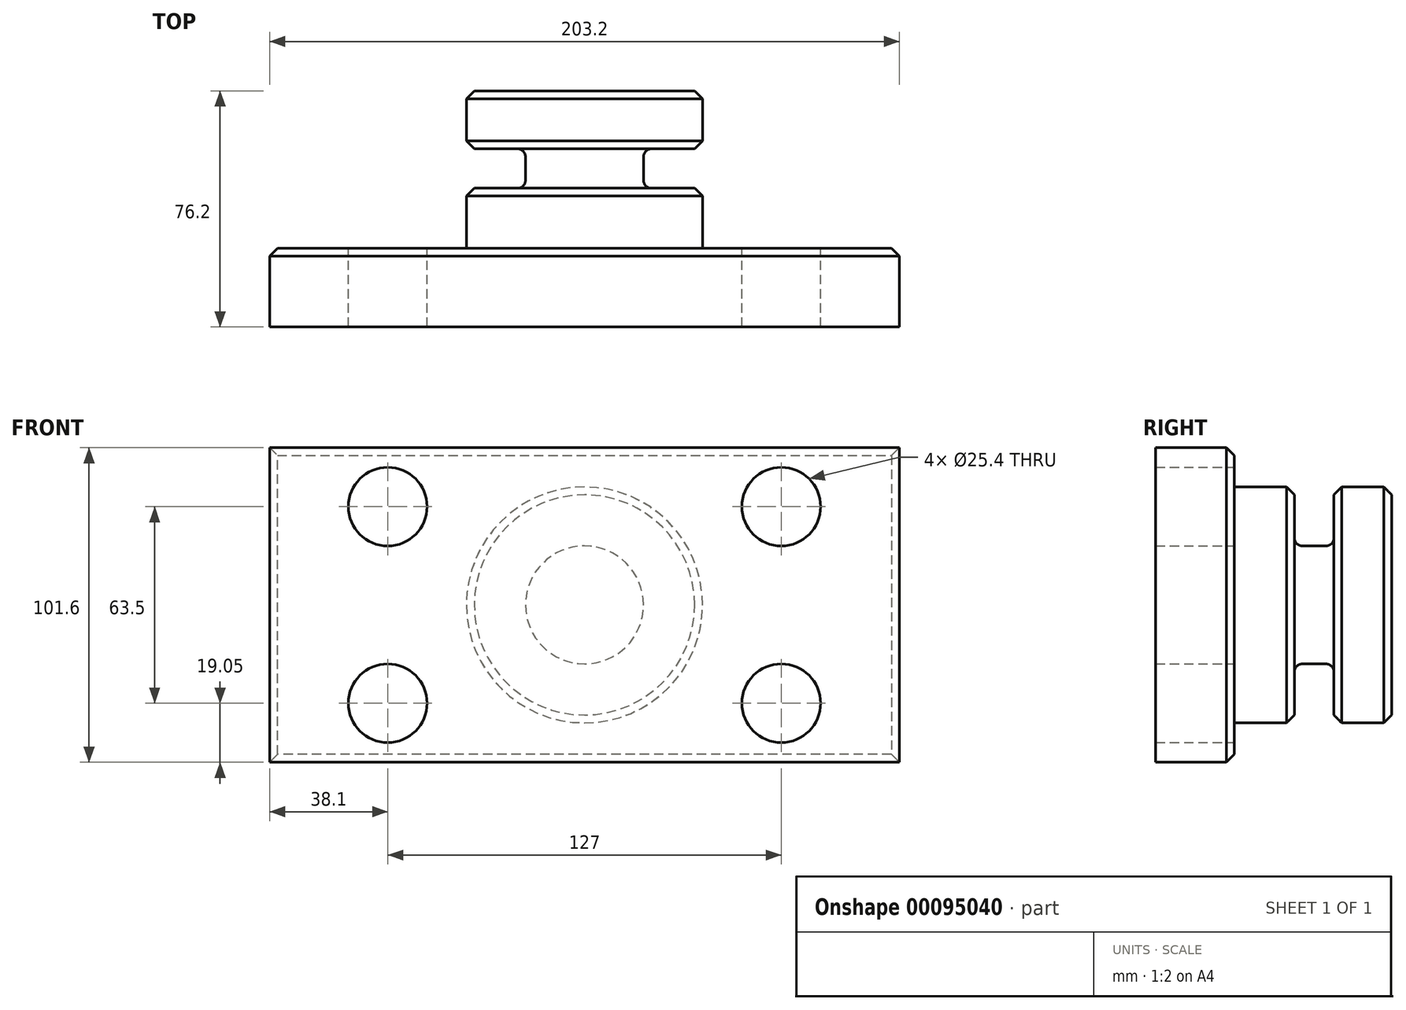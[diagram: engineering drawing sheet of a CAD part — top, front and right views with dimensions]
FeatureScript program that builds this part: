
annotation { "Feature Type Name" : "Feature", "Feature Type Description" : "" }
export const myFeature = defineFeature(function(context is Context, id is Id, definition is map)
    precondition{}
    {
        {
            var Q0;
            Q0=qCreatedBy(makeId("Front.planeOp"),FACE);
            var sketch = newSketch(context, id + "F0", { "sketchPlane" : qUnion([Q0])});
            skLineSegment(sketch, "E0.bottom", {"start": v(-101.6, 50.8) * mm, "end": v(101.6, 50.8) * mm});
            skLineSegment(sketch, "E0.top", {"start": v(-101.6, -50.8) * mm, "end": v(101.6, -50.8) * mm});
            skLineSegment(sketch, "E0.left", {"start": v(-101.6, 50.8) * mm, "end": v(-101.6, -50.8) * mm});
            skLineSegment(sketch, "E0.right", {"start": v(101.6, 50.8) * mm, "end": v(101.6, -50.8) * mm});
            skPoint(sketch, "E0.middle", {"position": v(0, 0) * mm});
            skSolve(sketch);
        }
        {
            var Q0;
            Q0 = qSketchRegion(id + "F0", true);
            extrude(context, id + "F1", {"entities" : qUnion([Q0]), "depth" : 25.4 * mm});
        }
        {
            var Q0;
            Q0=qCreatedBy(makeId("Front.planeOp"),FACE);
            var sketch = newSketch(context, id + "F2", { "sketchPlane" : qUnion([Q0])});
            skCircle(sketch, "E1", {"center": v(-63.5, 31.75) * mm, "radius": 12.7 * mm});
            skCircle(sketch, "E2", {"center": v(-63.5, -31.75) * mm, "radius": 12.7 * mm});
            skCircle(sketch, "E3", {"center": v(63.5, 31.75) * mm, "radius": 12.7 * mm});
            skCircle(sketch, "E4", {"center": v(63.5, -31.75) * mm, "radius": 12.7 * mm});
            skSolve(sketch);
        }
        {
            var Q0;
            Q0 = qSketchRegion(id + "F2", true);
            extrude(context, id + "F3", {"entities" : qUnion([Q0]), "operationType" : NewBodyOperationType.REMOVE, "depth" : 25.4 * mm});
        }
        {
            var Q0;
            Q0=qCreatedBy(makeId("Top.planeOp"),FACE);
            var sketch = newSketch(context, id + "F4", { "sketchPlane" : qUnion([Q0])});
            skLineSegment(sketch, "E5.bottom", {"start": v(0, 50.8) * mm, "end": v(-38.1, 50.8) * mm});
            skLineSegment(sketch, "E5.top", {"start": v(0, 0) * mm, "end": v(-38.1, 0) * mm});
            skLineSegment(sketch, "E5.left", {"start": v(0, 50.8) * mm, "end": v(0, 0) * mm});
            skLineSegment(sketch, "E5.right", {"start": v(-38.1, 50.8) * mm, "end": v(-38.1, 0) * mm});
            skSolve(sketch);
        }
        {
            var Q0;
            Q0 = qSketchRegion(id + "F4", true);
            var Q1;
            Q1=sQuery(id+"F4.wireOp",EDGE,"E5.left");
            revolve(context, id + "F5", {"operationType" : NewBodyOperationType.ADD, "entities" : qUnion([Q0]), "axis" : qUnion([Q1]), "revolveType" : RevolveType.FULL});
        }
        {
            var Q0;
            Q0=qCreatedBy(makeId("Top.planeOp"),FACE);
            var sketch = newSketch(context, id + "F6", { "sketchPlane" : qUnion([Q0])});
            skLineSegment(sketch, "E6.bottom", {"start": v(-44.45, 32.1) * mm, "end": v(-19.05, 32.1) * mm});
            skLineSegment(sketch, "E6.top", {"start": v(-44.45, 19.4) * mm, "end": v(-19.05, 19.4) * mm});
            skLineSegment(sketch, "E6.left", {"start": v(-44.45, 32.1) * mm, "end": v(-44.45, 19.4) * mm});
            skLineSegment(sketch, "E6.right", {"start": v(-19.05, 32.1) * mm, "end": v(-19.05, 19.4) * mm});
            skLineSegment(sketch, "E7", {"start": v(0, 0) * mm, "end": v(0, 134.13) * mm, "construction": true});
            skSolve(sketch);
        }
        {
            var Q0;
            Q0 = qSketchRegion(id + "F6", true);
            var Q1;
            Q1=sQuery(id+"F6.wireOp",EDGE,"E7");
            revolve(context, id + "F7", {"operationType" : NewBodyOperationType.REMOVE, "entities" : qUnion([Q0]), "axis" : qUnion([Q1]), "revolveType" : RevolveType.FULL, "oppositeDirection" : true});
        }
        {
            var Q0;
            Q0=makeQuery(id+"F5.opRevolve","SWEPT_EDGE",EDGE,{"disambiguationData":[OSD([sQuery(id+"F4.wireOp",EDGE,"E5.top"),sQuery(id+"F4.wireOp",EDGE,"E5.right")])]});
            var Q1;
            Q1=makeQuery(id+"F7.boolean.opBoolean","COPY",EDGE,{"derivedFrom":makeQuery(id+"F7.opRevolve","SWEPT_EDGE",EDGE,{"disambiguationData":[OSD([sQuery(id+"F6.wireOp",EDGE,"E6.top"),sQuery(id+"F6.wireOp",EDGE,"E6.right")])]})});
            var Q2;
            Q2=makeQuery(id+"F7.boolean.opBoolean","COPY",EDGE,{"derivedFrom":makeQuery(id+"F7.opRevolve","SWEPT_EDGE",EDGE,{"disambiguationData":[OSD([sQuery(id+"F6.wireOp",EDGE,"E6.bottom"),sQuery(id+"F6.wireOp",EDGE,"E6.right")])]})});
            fillet(context, id + "F8", {"entities" : qUnion([Q0, Q1, Q2]), "radius" : 2.54 * mm, "tangentPropagation" : true, "allowEdgeOverflow" : false});
        }
        {
            var Q0;
            Q0=makeQuery(id+"F5.opRevolve","SWEPT_EDGE",EDGE,{"disambiguationData":[OSD([sQuery(id+"F4.wireOp",EDGE,"E5.bottom"),sQuery(id+"F4.wireOp",EDGE,"E5.right")])]});
            var Q1;
            Q1=makeQuery(id+"F7.boolean.opBoolean","INTERSECT",EDGE,{"derivedFrom":[makeQuery(id+"F5.opRevolve","SWEPT_FACE",FACE,{"disambiguationData":[OSD([sQuery(id+"F4.wireOp",EDGE,"E5.right")])]}),makeQuery(id+"F7.opRevolve","SWEPT_FACE",FACE,{"disambiguationData":[OSD([sQuery(id+"F6.wireOp",EDGE,"E6.bottom")])]})]});
            var Q2;
            Q2=makeQuery(id+"F7.boolean.opBoolean","INTERSECT",EDGE,{"derivedFrom":[makeQuery(id+"F5.opRevolve","SWEPT_FACE",FACE,{"disambiguationData":[OSD([sQuery(id+"F4.wireOp",EDGE,"E5.right")])]}),makeQuery(id+"F7.opRevolve","SWEPT_FACE",FACE,{"disambiguationData":[OSD([sQuery(id+"F6.wireOp",EDGE,"E6.top")])]})]});
            var Q3;
            Q3=makeQuery(id+"F1.opExtrude","CAP_EDGE",EDGE,{"disambiguationData":[OSD([sQuery(id+"F0.wireOp",EDGE,"E0.left")])],"isStart":true});
            var Q4;
            Q4=makeQuery(id+"F1.opExtrude","CAP_EDGE",EDGE,{"disambiguationData":[OSD([sQuery(id+"F0.wireOp",EDGE,"E0.top")])],"isStart":true});
            var Q5;
            Q5=makeQuery(id+"F1.opExtrude","CAP_EDGE",EDGE,{"disambiguationData":[OSD([sQuery(id+"F0.wireOp",EDGE,"E0.bottom")])],"isStart":true});
            var Q6;
            Q6=makeQuery(id+"F1.opExtrude","CAP_EDGE",EDGE,{"disambiguationData":[OSD([sQuery(id+"F0.wireOp",EDGE,"E0.right")])],"isStart":true});
            chamfer(context, id + "F9", {"entities" : qUnion([Q0, Q1, Q2, Q3, Q4, Q5, Q6]), "width" : 2.54 * mm, "tangentPropagation" : true});
        }
    });
